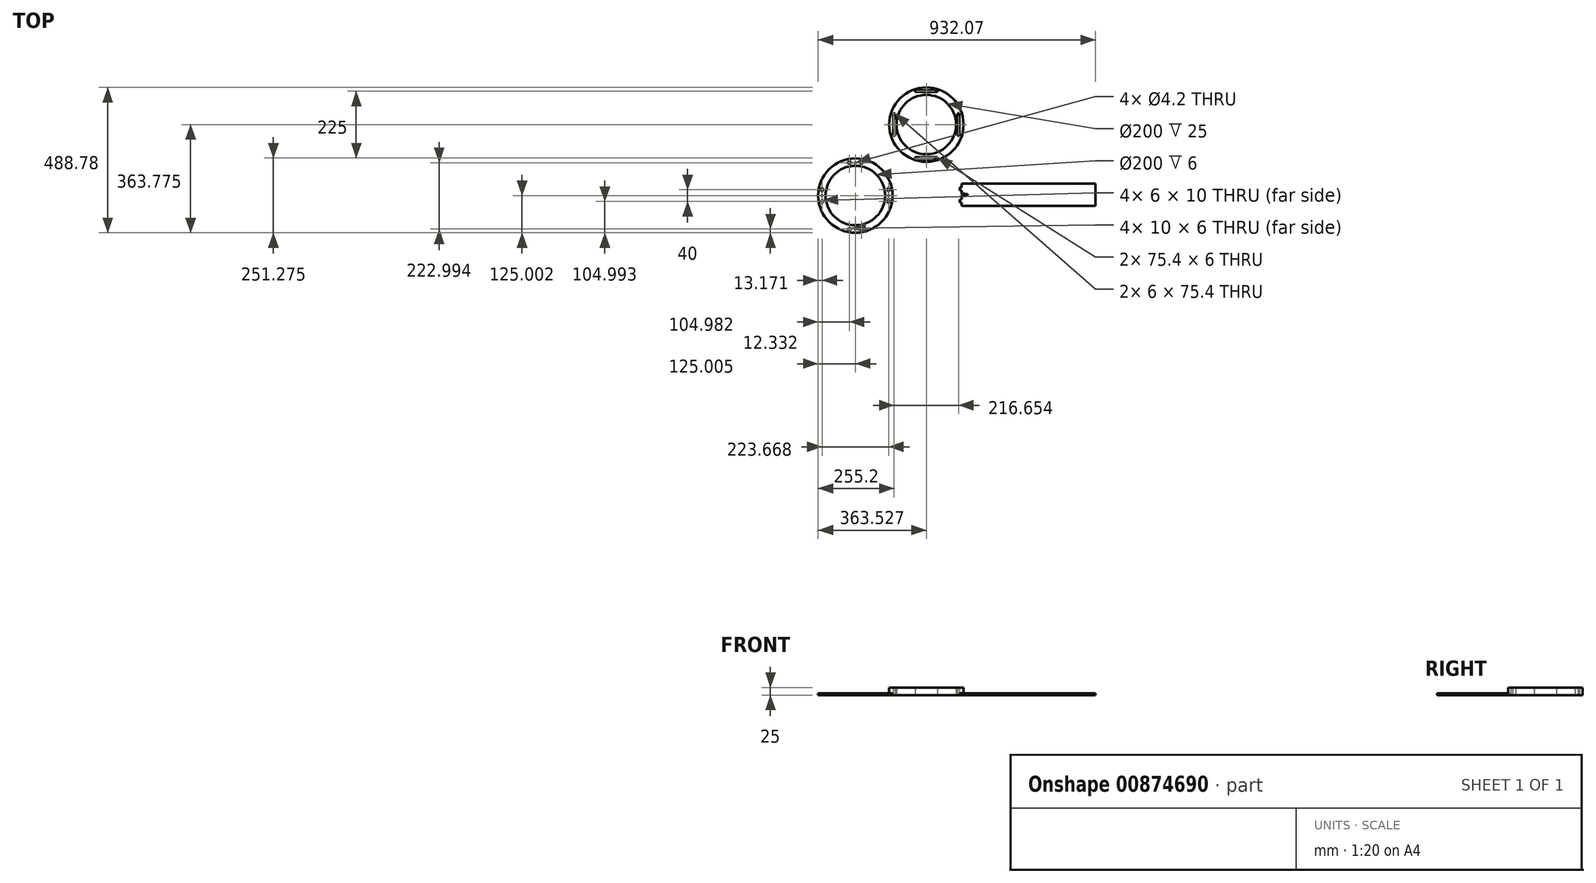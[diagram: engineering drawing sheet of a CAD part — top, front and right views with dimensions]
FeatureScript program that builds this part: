
annotation { "Feature Type Name" : "Feature", "Feature Type Description" : "" }
export const myFeature = defineFeature(function(context is Context, id is Id, definition is map)
    precondition{}
    {
        {
            var Q0;
            Q0=qCreatedBy(makeId("Top.planeOp"),FACE);
            var sketch = newSketch(context, id + "F0", { "sketchPlane" : qUnion([Q0])});
            skLineSegment(sketch, "E0", {"start": v(-53.83, 99.17) * mm, "end": v(-53.83, 86.6) * mm});
            skLineSegment(sketch, "E1", {"start": v(-53.83, 86.6) * mm, "end": v(-59.87, 86.6) * mm});
            skLineSegment(sketch, "E2.MirrorCS", {"start": v(-59.87, 86.6) * mm, "end": v(-59.87, 76.53) * mm});
            skLineSegment(sketch, "E3.MirrorCS", {"start": v(-59.87, 76.53) * mm, "end": v(-53.83, 76.53) * mm});
            skLineSegment(sketch, "E4.MirrorCS", {"start": v(-53.83, 76.53) * mm, "end": v(-53.83, 63.2) * mm});
            skLineSegment(sketch, "E5.MirrorCS", {"start": v(-53.83, 23.72) * mm, "end": v(-53.83, 36.3) * mm});
            skLineSegment(sketch, "E6.MirrorCS", {"start": v(-53.83, 36.3) * mm, "end": v(-59.87, 36.3) * mm});
            skLineSegment(sketch, "E7.MirrorCS", {"start": v(-59.87, 36.3) * mm, "end": v(-59.87, 46.36) * mm});
            skLineSegment(sketch, "E8.MirrorCS", {"start": v(-59.87, 46.36) * mm, "end": v(-53.83, 46.36) * mm});
            skLineSegment(sketch, "E9.MirrorCS", {"start": v(-53.83, 59.68) * mm, "end": v(-46.79, 59.68) * mm});
            skLineSegment(sketch, "E10.MirrorCS", {"start": v(-46.79, 59.68) * mm, "end": v(-46.79, 57.17) * mm});
            skLineSegment(sketch, "E11.MirrorCS", {"start": v(-46.79, 57.17) * mm, "end": v(-43.77, 57.17) * mm});
            skLineSegment(sketch, "E12.MirrorCS", {"start": v(-43.77, 57.17) * mm, "end": v(-43.77, 59.68) * mm});
            skLineSegment(sketch, "E13.MirrorCS", {"start": v(-43.77, 59.68) * mm, "end": v(-33.71, 59.68) * mm});
            skLineSegment(sketch, "E14.MirrorCS", {"start": v(-33.71, 63.2) * mm, "end": v(-33.71, 59.68) * mm});
            skLineSegment(sketch, "E15.MirrorCS", {"start": v(-43.77, 63.2) * mm, "end": v(-33.71, 63.2) * mm});
            skLineSegment(sketch, "E16.MirrorCS", {"start": v(-43.77, 65.72) * mm, "end": v(-43.77, 63.2) * mm});
            skLineSegment(sketch, "E17.MirrorCS", {"start": v(-46.79, 65.72) * mm, "end": v(-43.77, 65.72) * mm});
            skLineSegment(sketch, "E18.MirrorCS", {"start": v(-46.79, 63.2) * mm, "end": v(-46.79, 65.72) * mm});
            skLineSegment(sketch, "E19.MirrorCS", {"start": v(-53.83, 63.2) * mm, "end": v(-46.79, 63.2) * mm});
            skLineSegment(sketch, "E20.MirrorCS", {"start": v(-53.83, 46.36) * mm, "end": v(-53.83, 59.68) * mm});
            skLineSegment(sketch, "E21", {"start": v(-53.83, 99.17) * mm, "end": v(279.17, 99.17) * mm});
            skLineSegment(sketch, "E22", {"start": v(-53.83, 23.72) * mm, "end": v(279.17, 23.72) * mm});
            skLineSegment(sketch, "E23", {"start": v(279.17, 99.17) * mm, "end": v(396.17, 99.17) * mm});
            skLineSegment(sketch, "E24", {"start": v(396.17, 99.17) * mm, "end": v(396.17, 23.72) * mm});
            skLineSegment(sketch, "E25", {"start": v(279.17, 23.72) * mm, "end": v(396.17, 23.72) * mm});
            skSolve(sketch);
        }
        {
            var Q0;
            Q0 = qSketchRegion(id + "F0", true);
            extrude(context, id + "F1", {"entities" : qUnion([Q0]), "depth" : 6 * mm, "offsetDistance" : 25 * mm});
        }
        {
            var Q0;
            Q0=qCreatedBy(makeId("Top.planeOp"),FACE);
            var sketch = newSketch(context, id + "F2", { "sketchPlane" : qUnion([Q0])});
            skCircle(sketch, "E26", {"center": v(-410.9, 58.9) * mm, "radius": 125 * mm});
            skCircle(sketch, "E27", {"center": v(-410.9, 58.9) * mm, "radius": 100 * mm});
            skLineSegment(sketch, "E28", {"start": v(-410.9, 158.9) * mm, "end": v(-410.9, 58.9) * mm});
            skLineSegment(sketch, "E29", {"start": v(-410.9, 58.9) * mm, "end": v(-310.9, 58.9) * mm});
            skLineSegment(sketch, "E30.MirrorCS", {"start": v(-430.92, -50.77) * mm, "end": v(-425.92, -50.77) * mm});
            skCircle(sketch, "E31.MirrorC", {"center": v(-410.92, -53.77) * mm, "radius": 2.1 * mm});
            skLineSegment(sketch, "E32.MirrorCS", {"start": v(-395.92, -53.77) * mm, "end": v(-395.92, -50.77) * mm});
            skLineSegment(sketch, "E33.MirrorCS", {"start": v(-390.92, -50.77) * mm, "end": v(-385.92, -50.77) * mm});
            skLineSegment(sketch, "E34.MirrorCS", {"start": v(-395.92, -53.77) * mm, "end": v(-395.92, -56.77) * mm});
            skLineSegment(sketch, "E35.MirrorCS", {"start": v(-430.92, -50.77) * mm, "end": v(-435.92, -50.77) * mm});
            skLineSegment(sketch, "E36.MirrorCS", {"start": v(-435.92, -53.77) * mm, "end": v(-435.92, -56.77) * mm});
            skLineSegment(sketch, "E37.MirrorCS", {"start": v(-430.92, -56.77) * mm, "end": v(-425.92, -56.77) * mm});
            skLineSegment(sketch, "E38.MirrorCS", {"start": v(-425.92, -53.77) * mm, "end": v(-425.92, -56.77) * mm});
            skLineSegment(sketch, "E39.MirrorCS", {"start": v(-390.92, -56.77) * mm, "end": v(-395.92, -56.77) * mm});
            skLineSegment(sketch, "E40.MirrorCS", {"start": v(-385.92, -53.77) * mm, "end": v(-385.92, -50.77) * mm});
            skLineSegment(sketch, "E41.MirrorCS", {"start": v(-430.92, -56.77) * mm, "end": v(-435.92, -56.77) * mm});
            skLineSegment(sketch, "E42.MirrorCS", {"start": v(-435.92, -53.77) * mm, "end": v(-435.92, -50.77) * mm});
            skLineSegment(sketch, "E43.MirrorCS", {"start": v(-385.92, -53.77) * mm, "end": v(-385.92, -56.77) * mm});
            skLineSegment(sketch, "E44.MirrorCS", {"start": v(-390.92, -50.77) * mm, "end": v(-395.92, -50.77) * mm});
            skLineSegment(sketch, "E45.MirrorCS", {"start": v(-390.92, -56.77) * mm, "end": v(-385.92, -56.77) * mm});
            skLineSegment(sketch, "E46.MirrorCS", {"start": v(-425.92, -53.77) * mm, "end": v(-425.92, -50.77) * mm});
            skLineSegment(sketch, "E47.MirrorCS", {"start": v(-522.73, 73.9) * mm, "end": v(-519.73, 73.9) * mm});
            skLineSegment(sketch, "E48.MirrorCS", {"start": v(-519.73, 38.9) * mm, "end": v(-519.73, 43.9) * mm});
            skLineSegment(sketch, "E49.MirrorCS", {"start": v(-525.73, 38.9) * mm, "end": v(-525.73, 43.9) * mm});
            skLineSegment(sketch, "E50.MirrorCS", {"start": v(-522.73, 43.9) * mm, "end": v(-519.73, 43.9) * mm});
            skLineSegment(sketch, "E51.MirrorCS", {"start": v(-522.73, 33.9) * mm, "end": v(-519.73, 33.9) * mm});
            skLineSegment(sketch, "E52.MirrorCS", {"start": v(-522.73, 33.9) * mm, "end": v(-525.73, 33.9) * mm});
            skLineSegment(sketch, "E53.MirrorCS", {"start": v(-522.73, 83.9) * mm, "end": v(-525.73, 83.9) * mm});
            skLineSegment(sketch, "E54.MirrorCS", {"start": v(-522.73, 83.9) * mm, "end": v(-519.73, 83.9) * mm});
            skLineSegment(sketch, "E55.MirrorCS", {"start": v(-525.73, 78.9) * mm, "end": v(-525.73, 83.9) * mm});
            skLineSegment(sketch, "E56.MirrorCS", {"start": v(-519.73, 78.9) * mm, "end": v(-519.73, 83.9) * mm});
            skLineSegment(sketch, "E57.MirrorCS", {"start": v(-522.73, 43.9) * mm, "end": v(-525.73, 43.9) * mm});
            skLineSegment(sketch, "E58.MirrorCS", {"start": v(-522.73, 73.9) * mm, "end": v(-525.73, 73.9) * mm});
            skLineSegment(sketch, "E59.MirrorCS", {"start": v(-525.73, 78.9) * mm, "end": v(-525.73, 73.9) * mm});
            skLineSegment(sketch, "E60.MirrorCS", {"start": v(-519.73, 38.9) * mm, "end": v(-519.73, 33.9) * mm});
            skLineSegment(sketch, "E61.MirrorCS", {"start": v(-525.73, 38.9) * mm, "end": v(-525.73, 33.9) * mm});
            skLineSegment(sketch, "E62.MirrorCS", {"start": v(-519.73, 78.9) * mm, "end": v(-519.73, 73.9) * mm});
            skCircle(sketch, "E63.MirrorC", {"center": v(-522.73, 58.9) * mm, "radius": 2.1 * mm});
            skLineSegment(sketch, "E64", {"start": v(-410.9, 58.9) * mm, "end": v(-535.9, 58.9) * mm});
            skLineSegment(sketch, "E65.MirrorCS", {"start": v(-299.06, 33.9) * mm, "end": v(-302.06, 33.9) * mm});
            skLineSegment(sketch, "E66.MirrorCS", {"start": v(-299.06, 73.9) * mm, "end": v(-302.06, 73.9) * mm});
            skLineSegment(sketch, "E67.MirrorCS", {"start": v(-299.06, 83.9) * mm, "end": v(-302.06, 83.9) * mm});
            skLineSegment(sketch, "E68.MirrorCS", {"start": v(-299.06, 33.9) * mm, "end": v(-296.06, 33.9) * mm});
            skLineSegment(sketch, "E69.MirrorCS", {"start": v(-299.06, 73.9) * mm, "end": v(-296.06, 73.9) * mm});
            skLineSegment(sketch, "E70.MirrorCS", {"start": v(-299.06, 43.9) * mm, "end": v(-296.06, 43.9) * mm});
            skLineSegment(sketch, "E71.MirrorCS", {"start": v(-299.06, 83.9) * mm, "end": v(-296.06, 83.9) * mm});
            skLineSegment(sketch, "E72.MirrorCS", {"start": v(-299.06, 43.9) * mm, "end": v(-302.06, 43.9) * mm});
            skLineSegment(sketch, "E73.MirrorCS", {"start": v(-296.06, 78.9) * mm, "end": v(-296.06, 83.9) * mm});
            skLineSegment(sketch, "E74.MirrorCS", {"start": v(-302.06, 38.9) * mm, "end": v(-302.06, 33.9) * mm});
            skCircle(sketch, "E75.MirrorC", {"center": v(-299.06, 58.9) * mm, "radius": 2.1 * mm});
            skLineSegment(sketch, "E76.MirrorCS", {"start": v(-296.06, 78.9) * mm, "end": v(-296.06, 73.9) * mm});
            skLineSegment(sketch, "E77.MirrorCS", {"start": v(-302.06, 38.9) * mm, "end": v(-302.06, 43.9) * mm});
            skLineSegment(sketch, "E78.MirrorCS", {"start": v(-296.06, 38.9) * mm, "end": v(-296.06, 43.9) * mm});
            skLineSegment(sketch, "E79.MirrorCS", {"start": v(-296.06, 38.9) * mm, "end": v(-296.06, 33.9) * mm});
            skLineSegment(sketch, "E80.MirrorCS", {"start": v(-302.06, 78.9) * mm, "end": v(-302.06, 83.9) * mm});
            skLineSegment(sketch, "E81.MirrorCS", {"start": v(-302.06, 78.9) * mm, "end": v(-302.06, 73.9) * mm});
            skLineSegment(sketch, "E82.bottom", {"start": v(-425.92, 172.23) * mm, "end": v(-435.92, 172.23) * mm});
            skLineSegment(sketch, "E82.top", {"start": v(-425.92, 166.23) * mm, "end": v(-435.92, 166.23) * mm});
            skLineSegment(sketch, "E82.left", {"start": v(-425.92, 172.23) * mm, "end": v(-425.92, 166.23) * mm});
            skLineSegment(sketch, "E82.right", {"start": v(-435.92, 172.23) * mm, "end": v(-435.92, 166.23) * mm});
            skPoint(sketch, "E82.middle", {"position": v(-430.92, 169.23) * mm});
            skLineSegment(sketch, "E83.MirrorCS", {"start": v(-395.92, 172.23) * mm, "end": v(-395.92, 166.23) * mm});
            skLineSegment(sketch, "E84.MirrorCS", {"start": v(-395.92, 172.23) * mm, "end": v(-385.92, 172.23) * mm});
            skLineSegment(sketch, "E85.MirrorCS", {"start": v(-385.92, 172.23) * mm, "end": v(-385.92, 166.23) * mm});
            skLineSegment(sketch, "E86.MirrorCS", {"start": v(-395.92, 166.23) * mm, "end": v(-385.92, 166.23) * mm});
            skPoint(sketch, "E87.startSnap0", {"position": v(-390.92, 166.23) * mm});
            skCircle(sketch, "E88", {"center": v(-410.92, 169.23) * mm, "radius": 2.1 * mm});
            skLineSegment(sketch, "E89", {"start": v(-410.9, 158.9) * mm, "end": v(-410.9, 183.9) * mm});
            skSolve(sketch);
        }
        {
            var Q0;
            Q0 = qSketchRegion(id + "F2", true);
            extrude(context, id + "F3", {"entities" : qUnion([Q0]), "depth" : 6 * mm, "offsetDistance" : 25 * mm});
        }
        {
            var Q0;
            Q0 = qSketchRegion(id + "F2", true);
            extrude(context, id + "F4", {"entities" : qUnion([Q0]), "operationType" : NewBodyOperationType.REMOVE, "oppositeDirection" : true, "depth" : 25 * mm, "offsetDistance" : 25 * mm});
        }
        {
            var Q0;
            Q0=qCreatedBy(makeId("Top.planeOp"),FACE);
            var sketch = newSketch(context, id + "F5", { "sketchPlane" : qUnion([Q0])});
            skCircle(sketch, "E90", {"center": v(-172.37, 297.68) * mm, "radius": 125 * mm});
            skCircle(sketch, "E91", {"center": v(-172.37, 297.68) * mm, "radius": 100 * mm});
            skLineSegment(sketch, "E92", {"start": v(-172.37, 397.68) * mm, "end": v(-172.37, 297.68) * mm});
            skLineSegment(sketch, "E93", {"start": v(-172.37, 297.68) * mm, "end": v(-72.37, 297.68) * mm});
            skLineSegment(sketch, "E94", {"start": v(-172.37, 297.68) * mm, "end": v(-297.37, 297.68) * mm});
            skLineSegment(sketch, "E95", {"start": v(-172.37, 397.68) * mm, "end": v(-172.37, 422.68) * mm});
            skLineSegment(sketch, "E96.right", {"start": v(-50.32, 324.46) * mm, "end": v(-50.32, 324.68) * mm});
            skLineSegment(sketch, "E97.bottom", {"start": v(-67.05, 335.38) * mm, "end": v(-61.05, 335.38) * mm});
            skLineSegment(sketch, "E97.top", {"start": v(-67.05, 259.98) * mm, "end": v(-61.05, 259.98) * mm});
            skLineSegment(sketch, "E97.left", {"start": v(-67.05, 335.38) * mm, "end": v(-67.05, 259.98) * mm});
            skLineSegment(sketch, "E98", {"start": v(-72.37, 297.68) * mm, "end": v(-47.37, 297.68) * mm});
            skLineSegment(sketch, "E99", {"start": v(-61.05, 297.68) * mm, "end": v(-61.05, 259.98) * mm});
            skLineSegment(sketch, "E100", {"start": v(-61.05, 297.68) * mm, "end": v(-61.05, 335.38) * mm});
            skLineSegment(sketch, "E101.MirrorCS", {"start": v(-283.7, 297.68) * mm, "end": v(-283.7, 335.38) * mm});
            skLineSegment(sketch, "E102.MirrorCS", {"start": v(-277.7, 335.38) * mm, "end": v(-277.7, 259.98) * mm});
            skLineSegment(sketch, "E103.MirrorCS", {"start": v(-283.7, 297.68) * mm, "end": v(-283.7, 259.98) * mm});
            skLineSegment(sketch, "E104.MirrorCS", {"start": v(-277.7, 259.98) * mm, "end": v(-283.7, 259.98) * mm});
            skLineSegment(sketch, "E105.MirrorCS", {"start": v(-277.7, 335.38) * mm, "end": v(-283.7, 335.38) * mm});
            skLineSegment(sketch, "E106", {"start": v(-134.67, 410.18) * mm, "end": v(-134.67, 407.18) * mm});
            skLineSegment(sketch, "E107", {"start": v(-134.67, 410.18) * mm, "end": v(-134.67, 413.18) * mm});
            skLineSegment(sketch, "E108", {"start": v(-134.67, 413.18) * mm, "end": v(-172.37, 413.18) * mm});
            skLineSegment(sketch, "E109", {"start": v(-134.67, 407.18) * mm, "end": v(-172.37, 407.18) * mm});
            skLineSegment(sketch, "E110.MirrorCS", {"start": v(-210.07, 413.18) * mm, "end": v(-172.37, 413.18) * mm});
            skLineSegment(sketch, "E111.MirrorCS", {"start": v(-210.07, 407.18) * mm, "end": v(-172.37, 407.18) * mm});
            skLineSegment(sketch, "E112.MirrorCS", {"start": v(-210.07, 410.18) * mm, "end": v(-210.07, 413.18) * mm});
            skLineSegment(sketch, "E113.MirrorCS", {"start": v(-210.07, 410.18) * mm, "end": v(-210.07, 407.18) * mm});
            skLineSegment(sketch, "E114.MirrorCS", {"start": v(-134.67, 182.18) * mm, "end": v(-172.37, 182.18) * mm});
            skLineSegment(sketch, "E115.MirrorCS", {"start": v(-134.67, 188.18) * mm, "end": v(-172.37, 188.18) * mm});
            skLineSegment(sketch, "E116.MirrorCS", {"start": v(-210.07, 188.18) * mm, "end": v(-172.37, 188.18) * mm});
            skLineSegment(sketch, "E117.MirrorCS", {"start": v(-210.07, 182.18) * mm, "end": v(-172.37, 182.18) * mm});
            skLineSegment(sketch, "E118.MirrorCS", {"start": v(-210.07, 185.18) * mm, "end": v(-210.07, 182.18) * mm});
            skLineSegment(sketch, "E119.MirrorCS", {"start": v(-210.07, 185.18) * mm, "end": v(-210.07, 188.18) * mm});
            skLineSegment(sketch, "E120.MirrorCS", {"start": v(-134.67, 185.18) * mm, "end": v(-134.67, 182.18) * mm});
            skLineSegment(sketch, "E121.MirrorCS", {"start": v(-134.67, 185.18) * mm, "end": v(-134.67, 188.18) * mm});
            skSolve(sketch);
        }
        {
            var Q0;
            Q0 = qSketchRegion(id + "F5", true);
            extrude(context, id + "F6", {"entities" : qUnion([Q0]), "depth" : 25 * mm, "offsetDistance" : 25 * mm});
        }
    });
